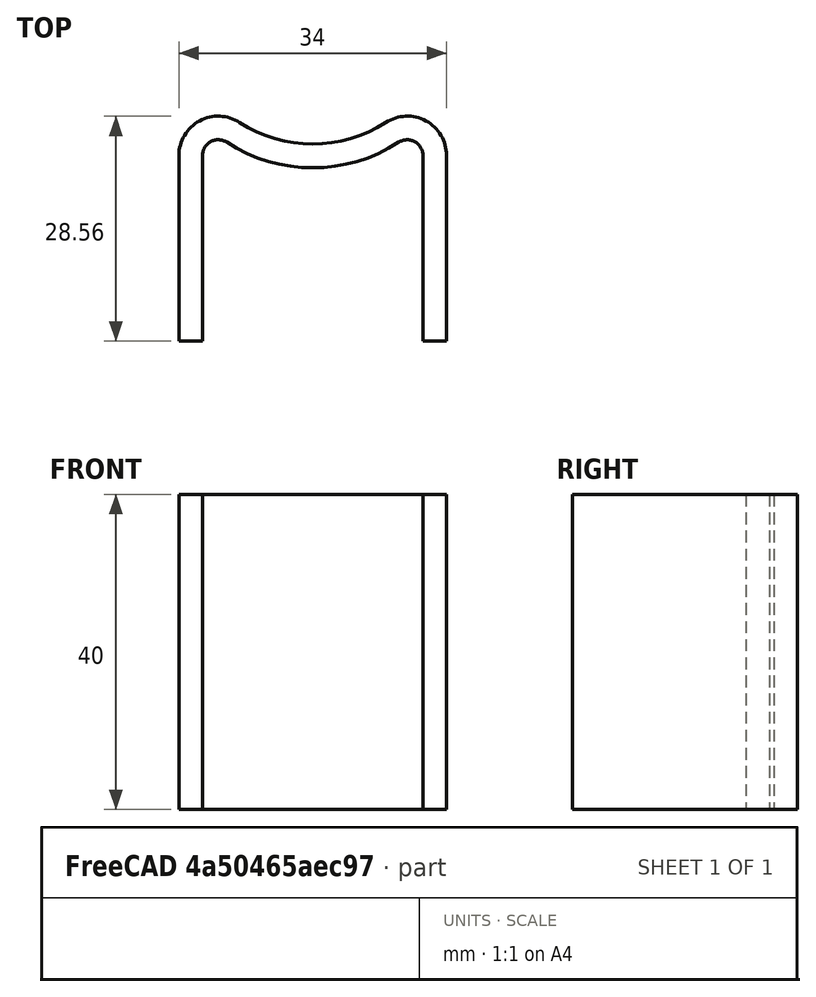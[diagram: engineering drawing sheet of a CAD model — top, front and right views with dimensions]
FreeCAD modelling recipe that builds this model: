
FCSTD DOCUMENT  (FreeCAD 0.18R4 (GitTag))
Label: door-rod-holder-small
License: All rights reserved
LicenseURL: http://en.wikipedia.org/wiki/All_rights_reserved
objects: Sketcher::SketchObject×1, PartDesign::Pad×1, PartDesign::Body×1
note: 4 computed .brp shape members not serialized (recipe doc carries the construction recipe); baked Part::Feature solids carry a one-line shape summary decoded from their .brp

FEATURE [Sketcher::SketchObject] Sketch
  MapMode = 5
  Support = -> [XY_Plane]
  sketch-geometry (12):
    g0: LineSegment StartX=1.5298e-11 StartY=0 StartZ=0 EndX=3 EndY=0 EndZ=0
    g1: LineSegment StartX=34 StartY=0 StartZ=0 EndX=34 EndY=23.561 EndZ=0
    g2: LineSegment StartX=1.5298e-11 StartY=23.561 StartZ=0 EndX=1.5298e-11 EndY=0 EndZ=0
    g3: LineSegment StartX=31 StartY=23.561 StartZ=0 EndX=31 EndY=0 EndZ=0
    g4: LineSegment StartX=3 StartY=0 StartZ=0 EndX=3 EndY=23.561 EndZ=0
    g5: LineSegment StartX=31 StartY=0 StartZ=0 EndX=34 EndY=0 EndZ=0
    g6: ArcOfCircle CenterX=5 CenterY=23.561 CenterZ=0 NormalX=0 NormalY=0 NormalZ=1 AngleXU=0 Radius=5 StartAngle=0.993864 EndAngle=3.14159
    g7: ArcOfCircle CenterX=17 CenterY=42.0001 CenterZ=0 NormalX=0 NormalY=0 NormalZ=1 AngleXU=0 Radius=17 StartAngle=4.13546 EndAngle=5.28932
    g8: ArcOfCircle CenterX=29 CenterY=23.561 CenterZ=0 NormalX=0 NormalY=0 NormalZ=1 AngleXU=0 Radius=5 StartAngle=6.28319 EndAngle=8.43091
    g9: ArcOfCircle CenterX=29 CenterY=23.561 CenterZ=0 NormalX=0 NormalY=0 NormalZ=1 AngleXU=0 Radius=2 StartAngle=1.68501e-07 EndAngle=2.14773
    g10: ArcOfCircle CenterX=17 CenterY=42.0001 CenterZ=0 NormalX=0 NormalY=0 NormalZ=1 AngleXU=0 Radius=20 StartAngle=4.13546 EndAngle=5.28932
    g11: ArcOfCircle CenterX=5 CenterY=23.561 CenterZ=0 NormalX=0 NormalY=0 NormalZ=1 AngleXU=0 Radius=2 StartAngle=0.993865 EndAngle=3.14159
  constraints (40):
    c: Coincident(g5,g1)
    c: Coincident(g2,g0)
    c: Horizontal(g0)
    c: Vertical(g1)
    c: Vertical(g2)
    c: Coincident(g0,g-1)
    c: Vertical(g3)
    c: Vertical(g4)
    c: Tangent(g0,g5)
    c: Coincident(g4,g0)
    c: Coincident(g3,g5)
    c: Coincident(g6,g2)
    c: Coincident(g7,g6)
    c: Coincident(g8,g7)
    c: Coincident(g8,g1)
    c: Coincident(g9,g3)
    c: Coincident(g10,g9)
    c: Coincident(g11,g10)
    c: Coincident(g11,g4)
    c: DistanceX(g3,g1) = 3
    c: DistanceX(g0,g0) = 3
    c: DistanceX(g0,g1) = 34
    c: Radius(g8) = 5
    c: Radius(g9) = 2
    c: Radius(g6) = 5
    c: Radius(g11) = 2
    c: Radius(g7) = 17
    c: Radius(g10) = 20
    c: Tangent(g6,g7)
    c: Tangent(g6,g2)
    c: DistanceY(g2,g2) = 23.561
    c: Tangent(g4,g11)
    c: Tangent(g10,g11)
    c: Equal(g4,g2)
    c: Tangent(g3,g9)
    c: Tangent(g10,g9)
    c: Equal(g3,g4)
    c: Equal(g1,g4)
    c: Tangent(g8,g1)
    c: Tangent(g8,g7)
FEATURE [PartDesign::Pad] Pad
  Length = 40
  Length2 = 100
  Profile = -> Sketch
  Refine = true
  Type = 0
FEATURE [PartDesign::Body] Body
  Group = -> [Sketch,Pad]
  Origin = -> Origin
  Tip = -> Pad
